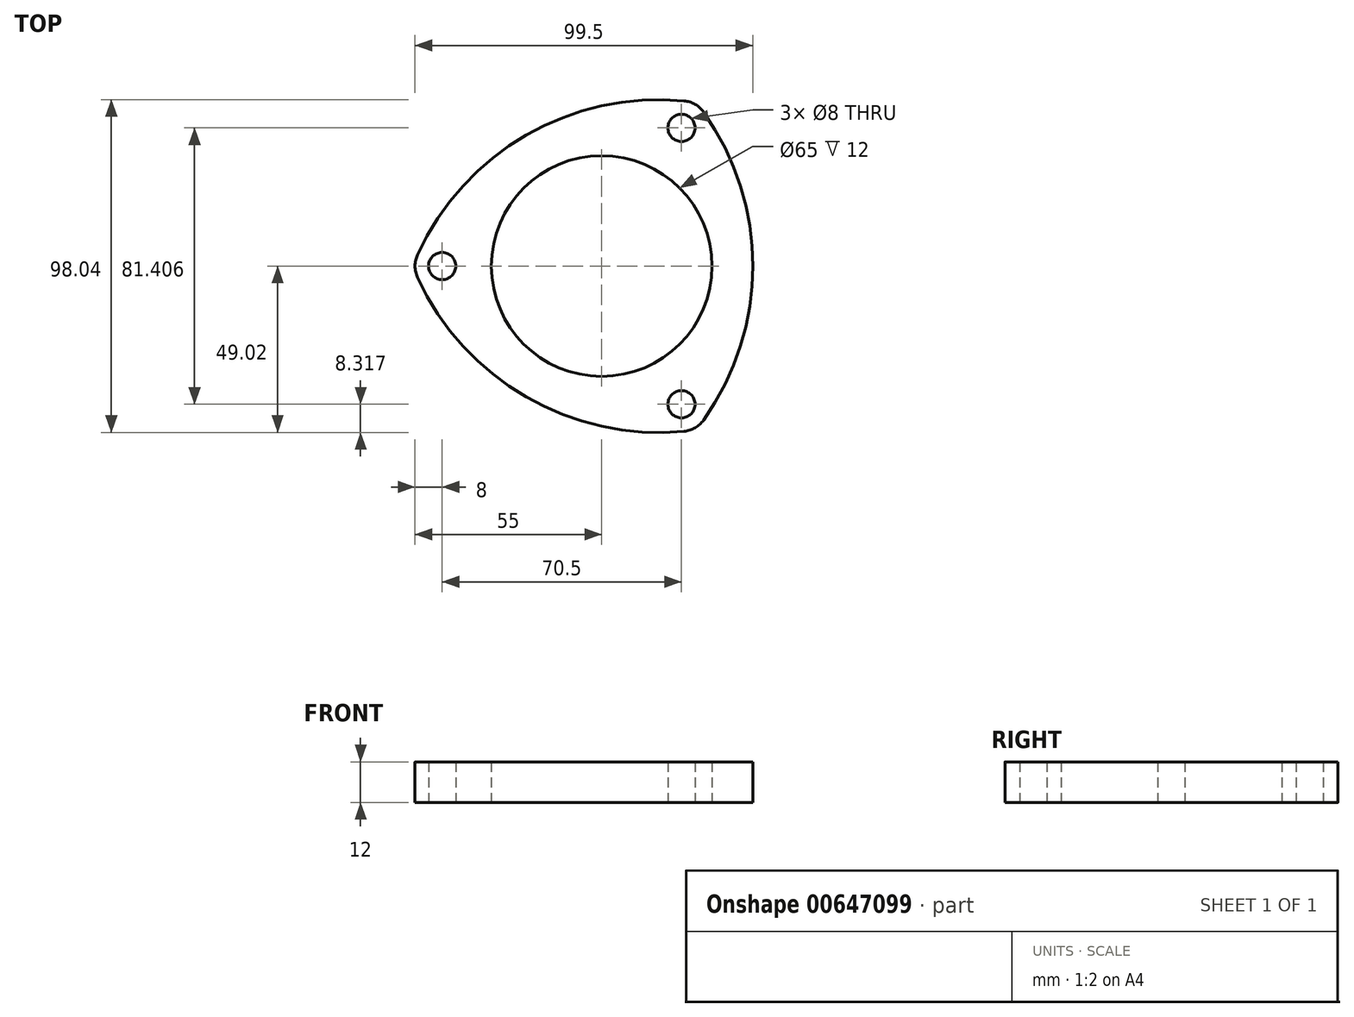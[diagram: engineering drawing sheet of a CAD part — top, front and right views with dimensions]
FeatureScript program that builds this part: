
annotation { "Feature Type Name" : "Feature", "Feature Type Description" : "" }
export const myFeature = defineFeature(function(context is Context, id is Id, definition is map)
    precondition{}
    {
        {
            var Q0;
            Q0=qCreatedBy(makeId("Top.planeOp"),FACE);
            var sketch = newSketch(context, id + "F0", { "sketchPlane" : qUnion([Q0])});
            skCircle(sketch, "E0", {"center": v(0, 0) * mm, "radius": 47 * mm, "construction": true});
            skCircle(sketch, "E1", {"center": v(0, 0) * mm, "radius": 32.5 * mm});
            skLineSegment(sketch, "E2", {"start": v(0, 0) * mm, "end": v(-47, 0) * mm, "construction": true});
            skLineSegment(sketch, "E3", {"start": v(0, 0) * mm, "end": v(23.5, 40.7) * mm, "construction": true});
            skLineSegment(sketch, "E4", {"start": v(0, 0) * mm, "end": v(23.5, -40.7) * mm, "construction": true});
            skCircle(sketch, "E5", {"center": v(-47, 0) * mm, "radius": 4 * mm});
            skCircle(sketch, "E6", {"center": v(23.5, 40.7) * mm, "radius": 4 * mm});
            skCircle(sketch, "E7", {"center": v(23.5, -40.7) * mm, "radius": 4 * mm});
            skCircle(sketch, "E8", {"center": v(23.5, 40.7) * mm, "radius": 8 * mm, "construction": true});
            skCircle(sketch, "E9", {"center": v(-47, 0) * mm, "radius": 8 * mm, "construction": true});
            skCircle(sketch, "E10", {"center": v(23.5, -40.7) * mm, "radius": 8 * mm, "construction": true});
            skArc(sketch, "E11", {"start": v(24.26, 48.67) * mm, "mid": v(-22.25, 38.54) * mm, "end": v(-54.28, 3.33) * mm});
            skArc(sketch, "E12", {"start": v(-54.28, -3.33) * mm, "mid": v(-22.25, -38.54) * mm, "end": v(24.26, -48.67) * mm});
            skArc(sketch, "E13", {"start": v(30.02, -45.34) * mm, "mid": v(44.5, 0) * mm, "end": v(30.02, 45.34) * mm});
            skArc(sketch, "E14", {"start": v(30.02, 45.34) * mm, "mid": v(27.5, 47.63) * mm, "end": v(24.26, 48.67) * mm});
            skArc(sketch, "E15", {"start": v(-54.28, 3.33) * mm, "mid": v(-55, 0) * mm, "end": v(-54.28, -3.33) * mm});
            skArc(sketch, "E16", {"start": v(24.26, -48.67) * mm, "mid": v(27.5, -47.63) * mm, "end": v(30.02, -45.34) * mm});
            skLineSegment(sketch, "E17", {"start": v(44.5, 0) * mm, "end": v(44.5, 65.84) * mm, "construction": true});
            skLineSegment(sketch, "E18", {"start": v(-55, 0) * mm, "end": v(-55, 63.87) * mm, "construction": true});
            skSolve(sketch);
        }
        {
            var Q0;
            Q0=makeQuery(id+"F0.imprint","IMPRINT",FACE,{"disambiguationData":[TD([[makeQuery(id+"F0.imprint","IMPRINT",EDGE,{"derivedFrom":sQuery(id+"F0.wireOp",EDGE,"E1")}),-1.0]])]});
            extrude(context, id + "F1", {"entities" : qUnion([Q0]), "depth" : 12 * mm, "offsetDistance" : 25 * mm});
        }
    });
